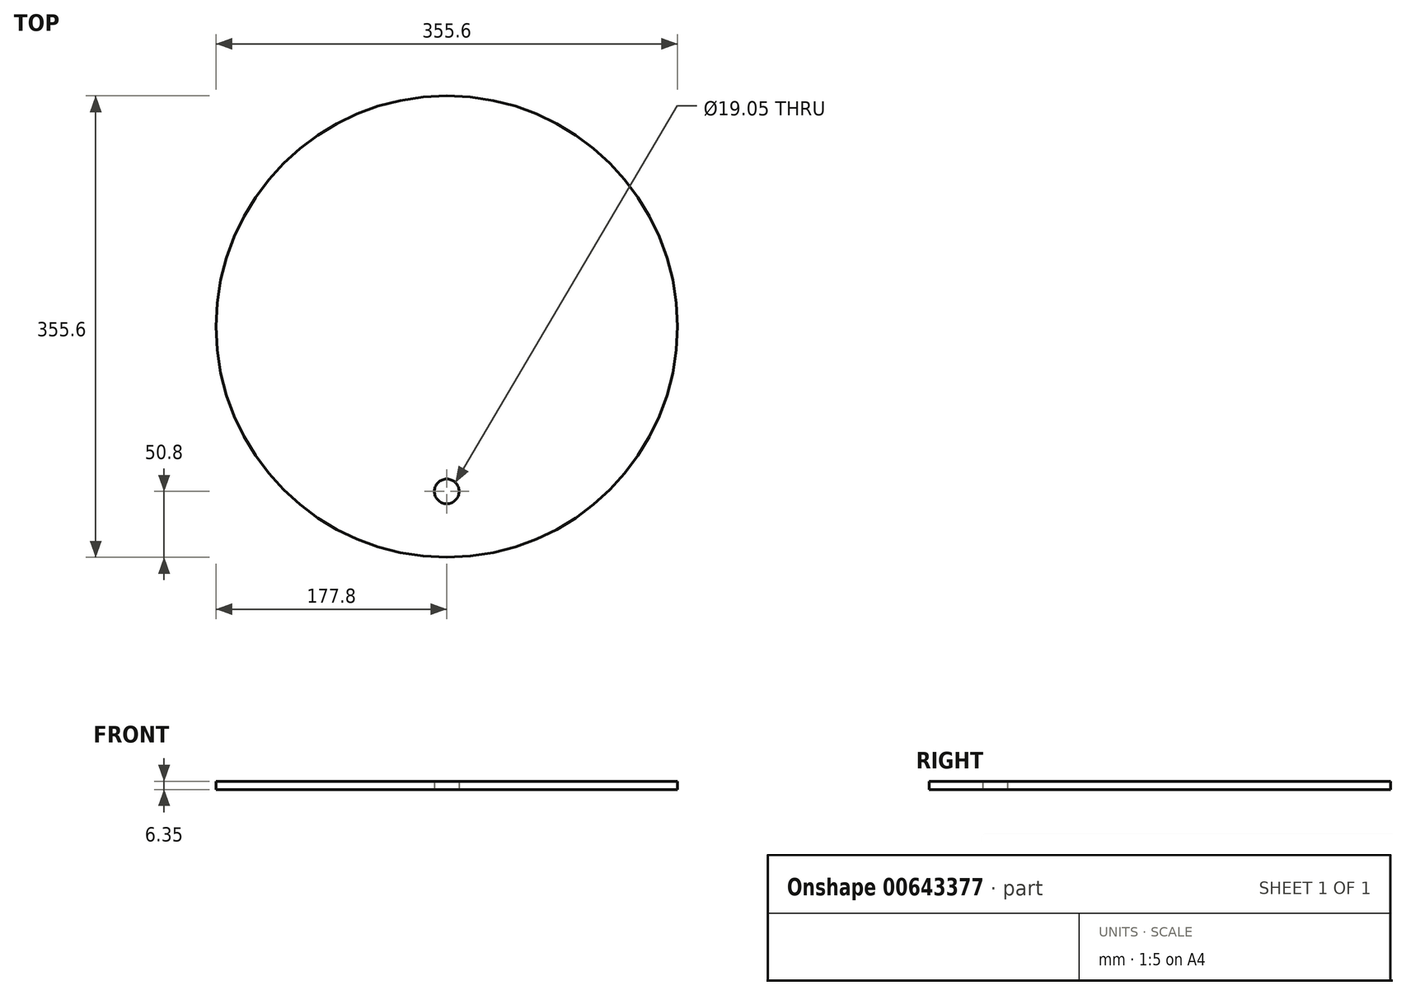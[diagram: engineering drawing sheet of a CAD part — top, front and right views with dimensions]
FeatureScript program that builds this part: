
annotation { "Feature Type Name" : "Feature", "Feature Type Description" : "" }
export const myFeature = defineFeature(function(context is Context, id is Id, definition is map)
    precondition{}
    {
        {
            var Q0;
            Q0=qCreatedBy(makeId("Top.planeOp"),FACE);
            var sketch = newSketch(context, id + "F0", { "sketchPlane" : qUnion([Q0])});
            skCircle(sketch, "E0", {"center": v(0, 0) * mm, "radius": 177.8 * mm});
            skLineSegment(sketch, "E1", {"start": v(-19.05, -177.8) * mm, "end": v(-19.05, -176.78) * mm});
            skLineSegment(sketch, "E2", {"start": v(19.05, -177.8) * mm, "end": v(19.05, -176.78) * mm});
            skCircle(sketch, "E3", {"center": v(0, -127) * mm, "radius": 9.53 * mm});
            skSolve(sketch);
        }
        {
            var Q0;
            Q0 = qSketchRegion(id + "F0", true);
            extrude(context, id + "F1", {"entities" : qUnion([Q0]), "depth" : 6.35 * mm, "offsetDistance" : 25.4 * mm});
        }
        {
            var Q0;
            Q0 = qSketchRegion(id + "F0", true);
            extrude(context, id + "F2", {"entities" : qUnion([Q0]), "operationType" : NewBodyOperationType.ADD, "depth" : 6.35 * mm, "offsetDistance" : 25.4 * mm});
        }
    });
